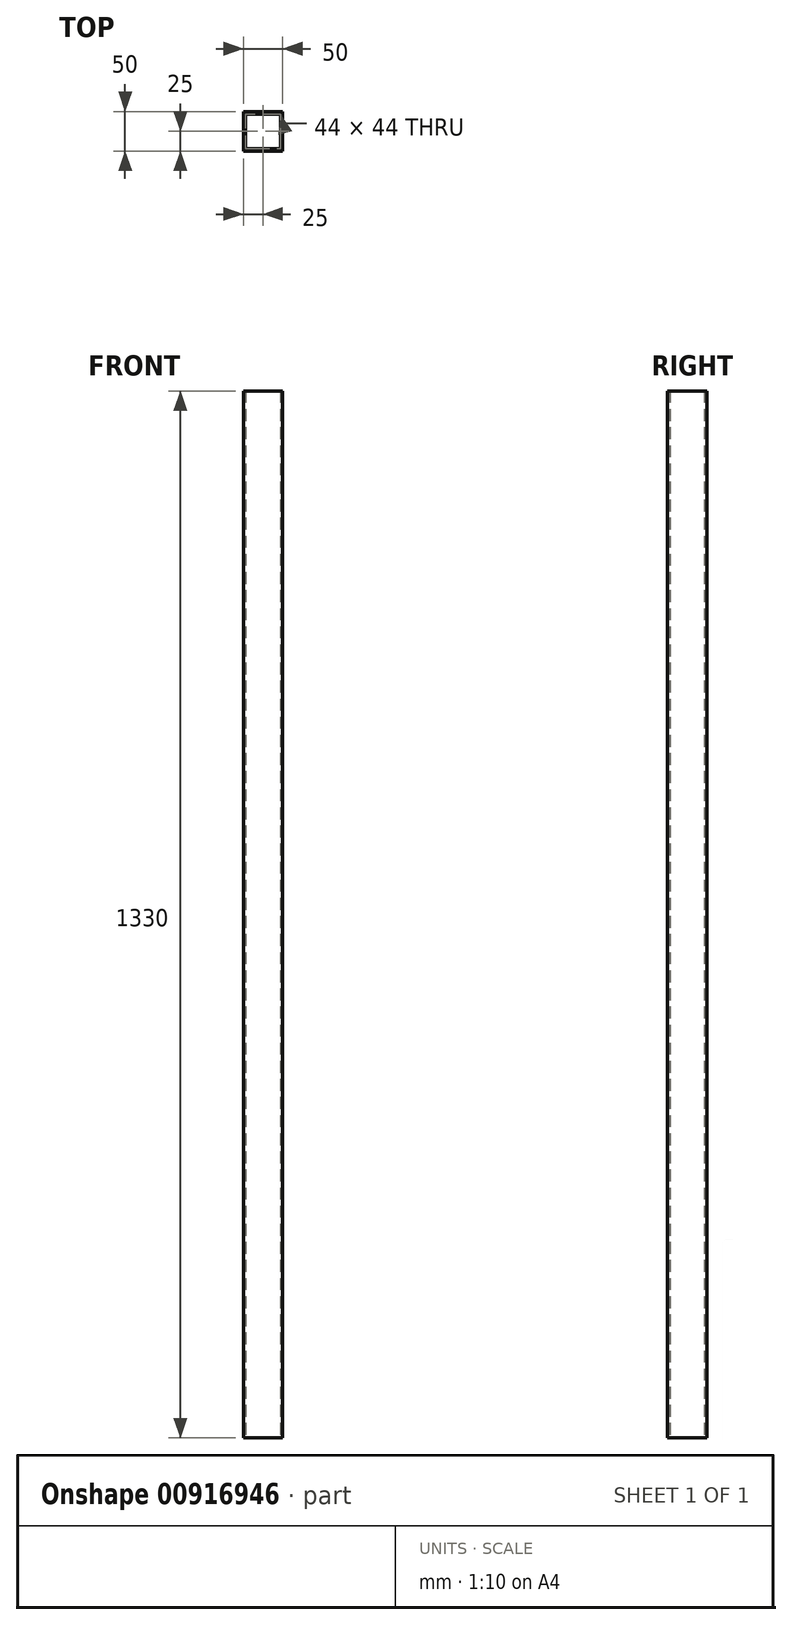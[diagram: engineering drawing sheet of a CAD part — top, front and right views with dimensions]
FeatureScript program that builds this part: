
annotation { "Feature Type Name" : "Feature", "Feature Type Description" : "" }
export const myFeature = defineFeature(function(context is Context, id is Id, definition is map)
    precondition{}
    {
        {
            var Q0;
            Q0=qCreatedBy(makeId("Top.planeOp"),FACE);
            var sketch = newSketch(context, id + "F0", { "sketchPlane" : qUnion([Q0])});
            skLineSegment(sketch, "E0.bottom", {"start": v(0, 0) * mm, "end": v(50, 0) * mm});
            skLineSegment(sketch, "E0.top", {"start": v(0, 50) * mm, "end": v(50, 50) * mm});
            skLineSegment(sketch, "E0.left", {"start": v(0, 0) * mm, "end": v(0, 50) * mm});
            skLineSegment(sketch, "E0.right", {"start": v(50, 0) * mm, "end": v(50, 50) * mm});
            skLineSegment(sketch, "E1.0", {"start": v(3, 3) * mm, "end": v(47, 3) * mm});
            skLineSegment(sketch, "E1.1", {"start": v(3, 3) * mm, "end": v(3, 47) * mm});
            skLineSegment(sketch, "E1.2", {"start": v(3, 47) * mm, "end": v(47, 47) * mm});
            skLineSegment(sketch, "E1.3", {"start": v(47, 3) * mm, "end": v(47, 47) * mm});
            skSolve(sketch);
        }
        {
            var Q0;
            Q0=makeQuery(id+"F0.imprint","IMPRINT",FACE,{"disambiguationData":[TD([[makeQuery(id+"F0.imprint","IMPRINT",EDGE,{"derivedFrom":sQuery(id+"F0.wireOp",EDGE,"E0.bottom")}),1.0]])]});
            extrude(context, id + "F1", {"entities" : qUnion([Q0]), "depth" : 1330 * mm, "offsetDistance" : 25 * mm});
        }
    });
